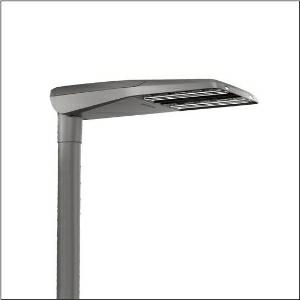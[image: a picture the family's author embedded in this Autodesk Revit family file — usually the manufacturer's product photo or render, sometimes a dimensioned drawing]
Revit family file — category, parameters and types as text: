
# Revit family: streetlight_sl_11_iq_midi___st1_2p1_0_5xc3g51e08me_ff57
name_source: partatom
category: Lighting Fixtures
units: mm (PartAtom-declared; Revit-internal decimal feet)

## family parameters
Cut with Voids When Loaded = No
Host = Face
Light Source = No
Part Type = Normal
Room Calculation Point = No
Round Connector Dimension = Use Diameter
Shared = No

## types (1)
- --- (1 x LED, 17750 lm, 121.7 W, 3000K)
    Apparent Load = 122 VA
    CIE Flux Codes = 31 68 95 100 100
    Color Rendering = 70
    Color Temperature = 3000K
    Default Elevation = 1800 mm
    Description = Streetlight SL 11 iQ midi, mast luminaire, primary light control with 3 zone facetted reflector, of plastic, silver coated, highly specular, primary optical cover: cover, of PMMA, transparent, light distribution: ST1.2P1.0, light emission: direct distribution, primary light characteristic: asymmetric, installation type: post-top, side-entry, lamps: LED, High Power LED, rated values: 17.750lm | 121,7W | 145,9lm/W (begin service life); end service life: 17.750lm | 129W; at 50% lumin. flux: 8.875lm | 56W | 158,5lm/W, colour temperature: 3000K, colour rendering: CRI > 70, light colour: 730, light setting 1 begin service life: 100% | 17.750lm | 121,7W | 145,9lm/W | 3.000K, light setting 1 end service life: 129W, further light settings possible, control: optimised constant luminous flux control (CLO 2.0), Desk-Remote (wireless, voltage-free reading and setting of iQ features in the workshop via application-optimized NFC function/RFID function), Light-Fading, Smart-Wire, Night-Set, Lumen-Switch, Temp-Guard, Auto-Match, with cable H07RN-F 3x 1.5mm², mains connection: 230..240V, AC, 50/60Hz, connection cable pre-assembled, cable length: 12,5m, luminaire housing, of diecast aluminium, powder-coated, SITECO metallic grey (DB 702S), please order mast flange separately, inclination adjustable without tools: 0°, 5°, 10°, 15° (post-top) | 0°, -5°, -10°, -15° (side-entry), sealing non-destructively replaceable, multi-level sealing system, length: 780mm, width: 376mm, height: 118mm, mast flange for spigot size: 42mm (side-entry): 5XC10008XM4, 60/48mm (side-entry/post-top): 5XC10108XM2, 76/60mm (side-entry/post-top): 5XC10108XM1, equipment: Power, protection rating (complete): IP66, insulation class (complete): insulation class II (safety insulation), certification: CE, ENEC, ENEC+, VDE, impact resistance: IK10, permissible operating ambient temperature for outdoor applications: -25..+50°C, standard-compliant lighting for roads and squares, Environmental Product Declaration (EPD) tested and certified by an independent institute, packaging unit: 1 piece

Light Distribution: ST1.2P1.0
    Height = 118 mm
    Lamp = 1 x LED
    Lamp Light Flux = 17750 lm
    Lamp Power = 121.7 W
    Lamp count = 1
    Length = 780 mm
    Luminous efficacy = 146 lm/W
    Manufacturer = Siteco
    ModVariant = No
    Model = 5XC3G51E08ME
    Number of Poles = 1
    OnlyDefault = Yes
    Power Factor = 1
    Product Name = Streetlight SL 11 iQ midi | ST1.2P1.0
    Product group = mast luminaire | pylon top
    ProductGroupID = 6100
    Protection Class = Protection class II
    Protection Degree = IP 66
    RLX_Detail_Level = 1
    RLX_Emergency_Light_Flux = 0 lm
    RLX_Emergency_Type = 0
    RLX_Emergency_Type_DB = No
    RlxData = <blob elided: 71189 chars, md5=c5626b58>
    Socket = socket
    Standby Power = 0 W
    System Light Flux = 17750 lm
    System Power = 122 W
    Type Comments = factory setting: luminous flux: 100 % | dim-lin: 254 | 544 mA
    Type Image = l_1005960.jpg
    URL = http://relux.com
    VarID = @adj_044169
    Voltage = 0 V
    Weight = 0.00 kg
    Width = 376 mm

## geometry (parser evidence)
native form markers: Blend x4, Sweep x10
no freeform markers — native parametric forms only
